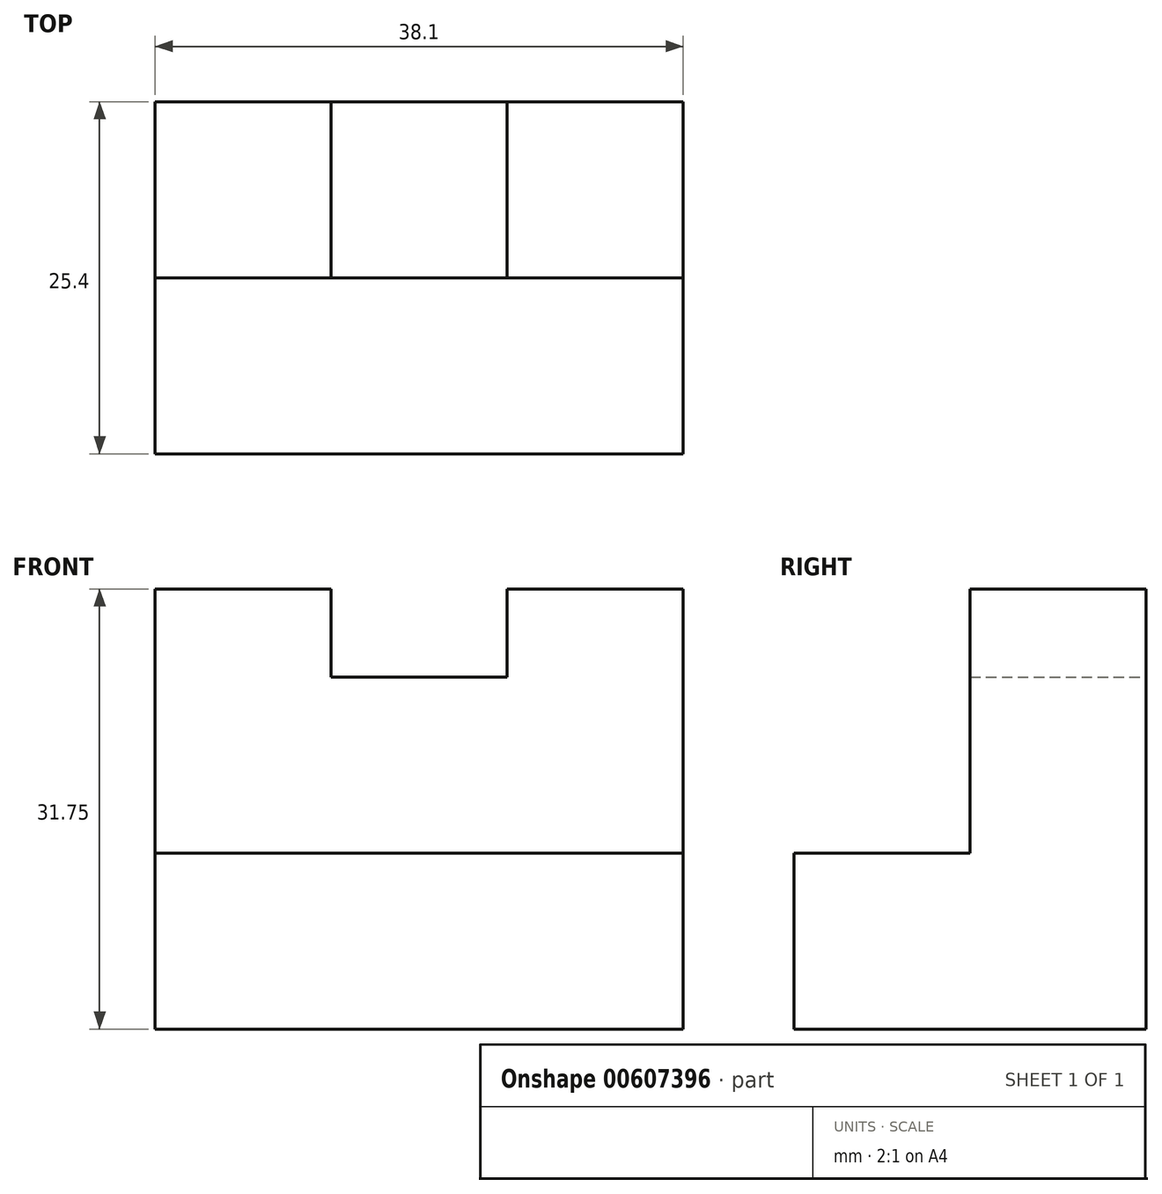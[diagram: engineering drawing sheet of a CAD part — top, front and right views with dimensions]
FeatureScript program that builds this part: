
annotation { "Feature Type Name" : "Feature", "Feature Type Description" : "" }
export const myFeature = defineFeature(function(context is Context, id is Id, definition is map)
    precondition{}
    {
        {
            var Q0;
            Q0=qCreatedBy(makeId("Right.planeOp"),FACE);
            var sketch = newSketch(context, id + "F0", { "sketchPlane" : qUnion([Q0])});
            skLineSegment(sketch, "E0", {"start": v(0, 0) * mm, "end": v(-25.4, 0) * mm});
            skLineSegment(sketch, "E1", {"start": v(-25.4, 0) * mm, "end": v(-25.4, 12.7) * mm});
            skLineSegment(sketch, "E2", {"start": v(-25.4, 12.7) * mm, "end": v(-12.7, 12.7) * mm});
            skLineSegment(sketch, "E3", {"start": v(-12.7, 12.7) * mm, "end": v(-12.7, 31.75) * mm});
            skLineSegment(sketch, "E4", {"start": v(-12.7, 31.75) * mm, "end": v(0, 31.75) * mm});
            skLineSegment(sketch, "E5", {"start": v(0, 31.75) * mm, "end": v(0, 0) * mm});
            skSolve(sketch);
        }
        {
            var Q0;
            Q0=makeQuery(id+"F0.imprint","IMPRINT",FACE,{"disambiguationData":[TD([[makeQuery(id+"F0.imprint","IMPRINT",EDGE,{"derivedFrom":sQuery(id+"F0.wireOp",EDGE,"E0")}),-1.0]])]});
            extrude(context, id + "F1", {"entities" : qUnion([Q0]), "depth" : 38.1 * mm, "offsetDistance" : 25.4 * mm});
        }
        {
            var Q0;
            Q0=makeQuery(id+"F1.opExtrude","SWEPT_FACE",FACE,{"disambiguationData":[OSD([sQuery(id+"F0.wireOp",EDGE,"E4")])]});
            var sketch = newSketch(context, id + "F2", { "sketchPlane" : qUnion([Q0])});
            skLineSegment(sketch, "E6", {"start": v(19.05, -12.7) * mm, "end": v(12.7, -12.7) * mm});
            skLineSegment(sketch, "E7", {"start": v(12.7, -12.7) * mm, "end": v(25.4, -12.7) * mm});
            skLineSegment(sketch, "E8", {"start": v(25.4, -12.7) * mm, "end": v(25.4, 0) * mm});
            skLineSegment(sketch, "E9", {"start": v(25.4, 0) * mm, "end": v(12.7, 0) * mm});
            skLineSegment(sketch, "E10", {"start": v(12.7, 0) * mm, "end": v(12.7, -12.7) * mm});
            skSolve(sketch);
        }
        {
            var Q0;
            {var subQ0=sQuery(id+"F2.wireOp",EDGE,"E8");Q0=makeQuery(id+"F2.imprint","IMPRINT",FACE,{"disambiguationData":[TD([[makeQuery(id+"F2.imprint","IMPRINT",EDGE,{"derivedFrom":subQ0}),1.0]])]});}
            extrude(context, id + "F3", {"entities" : qUnion([Q0]), "operationType" : NewBodyOperationType.REMOVE, "oppositeDirection" : true, "depth" : 6.35 * mm, "offsetDistance" : 25.4 * mm});
        }
    });
